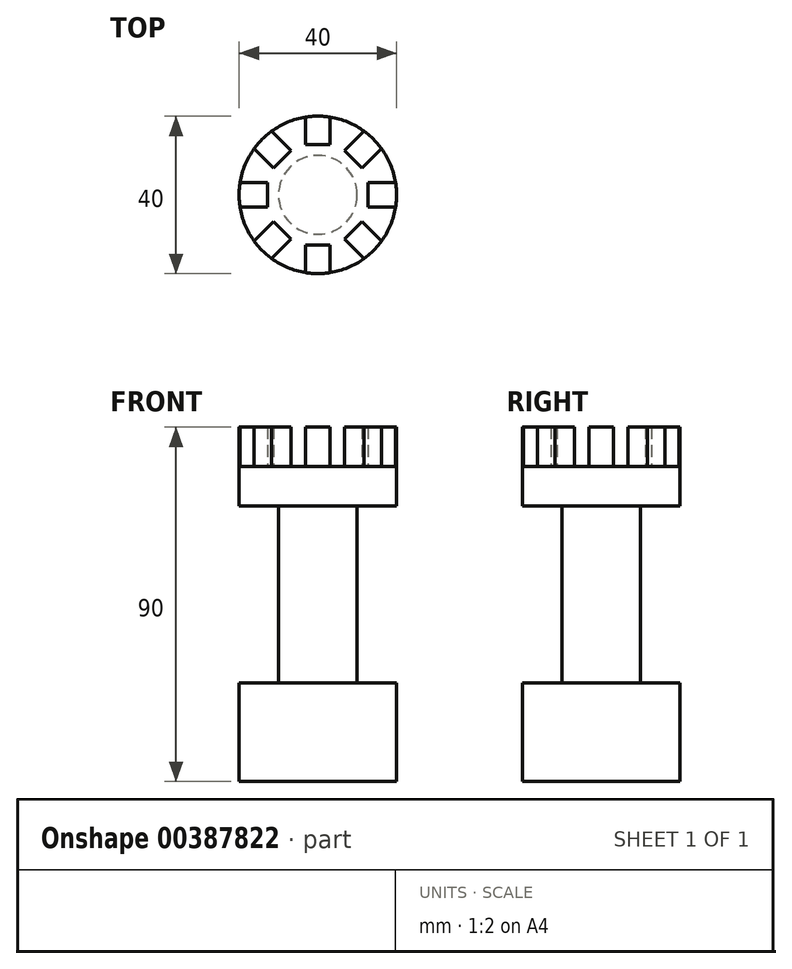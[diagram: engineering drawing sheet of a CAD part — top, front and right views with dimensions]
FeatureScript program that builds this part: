
annotation { "Feature Type Name" : "Feature", "Feature Type Description" : "" }
export const myFeature = defineFeature(function(context is Context, id is Id, definition is map)
    precondition{}
    {
        {
            var Q0;
            Q0=qCreatedBy(makeId("Front.planeOp"),FACE);
            var sketch = newSketch(context, id + "F0", { "sketchPlane" : qUnion([Q0])});
            skLineSegment(sketch, "E0", {"start": v(0, 66.6) * mm, "end": v(0, -66.37) * mm, "construction": true});
            skLineSegment(sketch, "E1", {"start": v(0, 0) * mm, "end": v(0, 40) * mm});
            skLineSegment(sketch, "E2", {"start": v(0, 40) * mm, "end": v(20, 40) * mm});
            skLineSegment(sketch, "E3", {"start": v(20, 40) * mm, "end": v(20, 30) * mm});
            skLineSegment(sketch, "E4", {"start": v(20, 30) * mm, "end": v(10, 30) * mm});
            skLineSegment(sketch, "E5", {"start": v(10, 30) * mm, "end": v(10, -15) * mm});
            skLineSegment(sketch, "E6", {"start": v(10, -15) * mm, "end": v(20, -15) * mm});
            skLineSegment(sketch, "E7", {"start": v(20, -15) * mm, "end": v(20, -40) * mm});
            skLineSegment(sketch, "E8", {"start": v(20, -40) * mm, "end": v(0, -40) * mm});
            skLineSegment(sketch, "E9", {"start": v(0, -40) * mm, "end": v(0, 0) * mm});
            skSolve(sketch);
        }
        {
            var Q0;
            Q0 = qSketchRegion(id + "F0", true);
            var Q1;
            Q1=sQuery(id+"F0.wireOp",EDGE,"E0");
            revolve(context, id + "F1", {"entities" : qUnion([Q0]), "axis" : qUnion([Q1]), "revolveType" : RevolveType.FULL});
        }
        {
            var Q0;
            Q0=makeQuery(id+"F1.opRevolve","SWEPT_FACE",FACE,{"disambiguationData":[OSD([sQuery(id+"F0.wireOp",EDGE,"E2")])]});
            var sketch = newSketch(context, id + "F2", { "sketchPlane" : qUnion([Q0])});
            skLineSegment(sketch, "E10", {"start": v(-3.14, 19.75) * mm, "end": v(-3.14, 12.75) * mm});
            skLineSegment(sketch, "E11", {"start": v(-3.14, 12.75) * mm, "end": v(3.14, 12.75) * mm});
            skLineSegment(sketch, "E12", {"start": v(3.14, 12.75) * mm, "end": v(3.14, 19.75) * mm});
            skArc(sketch, "E13", {"start": v(3.14, 19.75) * mm, "mid": v(0, 20) * mm, "end": v(-3.14, 19.75) * mm});
            skSolve(sketch);
        }
        {
            var Q0;
            Q0 = qSketchRegion(id + "F2", true);
            extrude(context, id + "F3", {"entities" : qUnion([Q0]), "operationType" : NewBodyOperationType.ADD, "depth" : 10 * mm});
        }
        {
            var Q0;
            Q0=makeQuery(id+"F1.opRevolve","SWEPT_BODY",BODY,{"disambiguationData":[OSD([sQuery(id+"F0.wireOp",EDGE,"E1"),sQuery(id+"F0.wireOp",EDGE,"E2"),sQuery(id+"F0.wireOp",EDGE,"E3"),sQuery(id+"F0.wireOp",EDGE,"E4"),sQuery(id+"F0.wireOp",EDGE,"E5"),sQuery(id+"F0.wireOp",EDGE,"E6"),sQuery(id+"F0.wireOp",EDGE,"E7"),sQuery(id+"F0.wireOp",EDGE,"E8"),sQuery(id+"F0.wireOp",EDGE,"E9")])]});
            var Q1;
            Q1=makeQuery(id+"F3.boolean.opBoolean","MERGE",FACE,{"derivedFrom":[makeQuery(id+"F1.opRevolve","SWEPT_FACE",FACE,{"disambiguationData":[OSD([sQuery(id+"F0.wireOp",EDGE,"E3")])]}),makeQuery(id+"F3.opExtrude","SWEPT_FACE",FACE,{"disambiguationData":[OSD([sQuery(id+"F2.wireOp",EDGE,"E13")])]})]});
            circularPattern(context, id + "F4", {"entities" : qUnion([Q0]), "axis" : qUnion([Q1]), "angle" : 360 * degree, "instanceCount" : 8, "equalSpace" : true});
        }
    });
